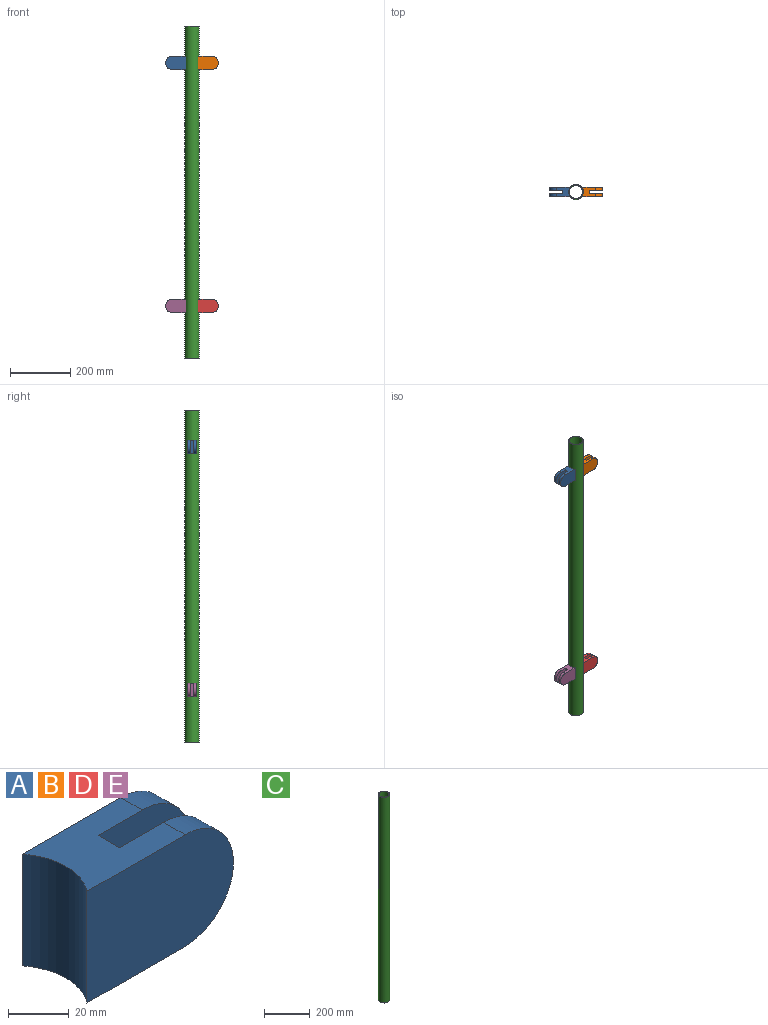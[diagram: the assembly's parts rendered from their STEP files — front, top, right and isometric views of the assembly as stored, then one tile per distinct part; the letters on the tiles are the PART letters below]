
ASSEMBLY  parts=5 mates=4
PART A: 10 faces, bbox 68.2x30x45 mm
  f0: plane 45x43mm, normal (0,-1,0), area 1717.7mm2, adj f5,f6,f7,f9
  f1: plane 68.22x45mm, normal (0,1,0), area 2852.8mm2, adj f4,f6,f7,f9
  f2: plane 68.22x45mm, normal (0,-1,0), area 2852.8mm2, adj f4,f6,f7,f8
  f3: plane 45x43mm, normal (0,1,0), area 1717.7mm2, adj f5,f6,f7,f8
  f4: cylinder r=24.15mm len=45mm, axis (0,0,-1), area 1456.6mm2, adj f1,f2,f6,f7
  f5: plane 45x10mm, normal (1,0,0), area 450mm2, adj f0,f3,f6,f7
  f6: plane 45.72x30mm, normal (0,0,1), area 1059.7mm2, adj f0,f1,f2,f3,f4,f5,f8,f9
  f7: plane 45.72x30mm, normal (0,0,-1), area 1059.7mm2, adj f0,f1,f2,f3,f4,f5,f8,f9
  f8: cylinder r=22.5mm len=45mm, axis (0,-1,0), area 706.9mm2, adj f2,f3,f6,f7
  f9: cylinder r=22.5mm len=45mm, axis (0,-1,0), area 706.9mm2, adj f0,f1,f6,f7
PART B: same geometry as A
PART C: 4 faces, bbox 48.3x48.3x1100 mm
  f0: cylinder r=22.15mm len=1100mm, axis (0,0,-1), area 153089.8mm2, adj f2,f3
  f1: cylinder r=24.15mm len=1100mm, axis (0,0,-1), area 166912.8mm2, adj f2,f3
  f2: plane 48.3x48.3mm, normal (0,0,1), area 290.9mm2, adj f0,f1
  f3: plane 48.3x48.3mm, normal (0,0,-1), area 290.9mm2, adj f0,f1
PART D: same geometry as A
PART E: same geometry as A
PLACE A rot(axis=(0,0,1),180deg) t=(0,0,955)mm
PLACE B rot(axis=(1,0,0),180deg) t=(0,0,1000)mm
PLACE C at identity fixed
PLACE D t=(0,0,150)mm
PLACE E rot(axis=(0,0,1),180deg) t=(0,0,150)mm
MATE fastened A.f4 <-> C.f1  axis (0,0,-1) through (0,0,977.5)mm
MATE fastened C.f1 <-> D.f4  axis (0,0,-1) through (0,0,550)mm
MATE fastened B.f4 <-> C.f1  axis (0,0,1) through (0,0,977.5)mm
MATE fastened E.f4 <-> C.f1  axis (0,0,-1) through (0,0,172.5)mm
